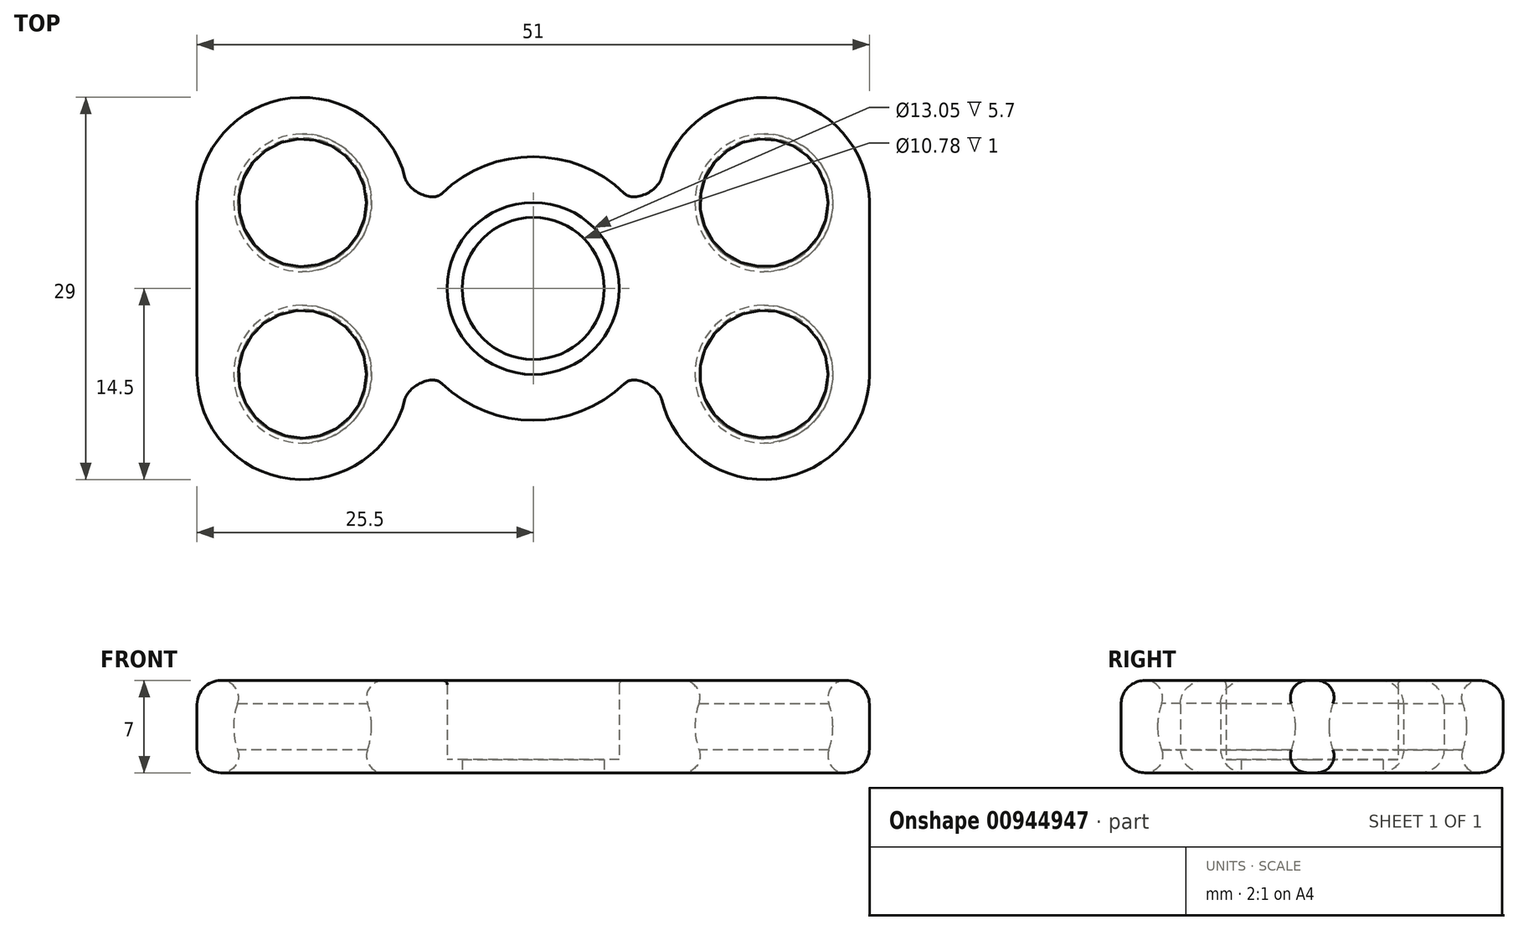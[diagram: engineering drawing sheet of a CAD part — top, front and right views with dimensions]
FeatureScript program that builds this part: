
annotation { "Feature Type Name" : "Feature", "Feature Type Description" : "" }
export const myFeature = defineFeature(function(context is Context, id is Id, definition is map)
    precondition{}
    {
        {
            var Q0;
            Q0=qCreatedBy(makeId("Top.planeOp"),FACE);
            var sketch = newSketch(context, id + "F0", { "sketchPlane" : qUnion([Q0])});
            skCircle(sketch, "E0", {"center": v(0, 0) * mm, "radius": 6.53 * mm});
            skArc(sketch, "E1", {"start": v(6.91, 7.23) * mm, "mid": v(0, 10) * mm, "end": v(-6.91, 7.23) * mm});
            skCircle(sketch, "E2", {"center": v(17.5, 6.5) * mm, "radius": 2.5 * mm});
            skCircle(sketch, "E3", {"center": v(17.5, -6.5) * mm, "radius": 2.5 * mm});
            skArc(sketch, "E4", {"start": v(9.73, -8.38) * mm, "mid": v(18.45, -14.44) * mm, "end": v(25.5, -6.5) * mm});
            skLineSegment(sketch, "E5", {"start": v(25.5, 6.5) * mm, "end": v(25.5, -6.5) * mm});
            skArc(sketch, "E6", {"start": v(7.68, 6.95) * mm, "mid": v(8.76, 7.29) * mm, "end": v(9.59, 8.07) * mm});
            skArc(sketch, "E7", {"start": v(9.59, -8.07) * mm, "mid": v(8.76, -7.29) * mm, "end": v(7.68, -6.95) * mm});
            skArc(sketch, "E8.trimOffspring", {"start": v(25.5, 6.5) * mm, "mid": v(18.45, 14.44) * mm, "end": v(9.73, 8.38) * mm});
            skLineSegment(sketch, "E9", {"start": v(0, 15.27) * mm, "end": v(0, -14.8) * mm});
            skPoint(sketch, "E10.visualSharp", {"position": v(7.18, 6.96) * mm});
            skArc(sketch, "E10.filletArc", {"start": v(6.91, 7.23) * mm, "mid": v(7.27, 7) * mm, "end": v(7.68, 6.95) * mm});
            skPoint(sketch, "E11.visualSharp", {"position": v(9.7, 8.24) * mm});
            skArc(sketch, "E11.filletArc", {"start": v(9.59, 8.07) * mm, "mid": v(9.67, 8.22) * mm, "end": v(9.73, 8.38) * mm});
            skPoint(sketch, "E12.visualSharp", {"position": v(7.18, -6.96) * mm});
            skArc(sketch, "E12.filletArc", {"start": v(7.68, -6.95) * mm, "mid": v(7.27, -7) * mm, "end": v(6.91, -7.23) * mm});
            skPoint(sketch, "E13.visualSharp", {"position": v(9.7, -8.24) * mm});
            skArc(sketch, "E13.filletArc", {"start": v(9.73, -8.38) * mm, "mid": v(9.67, -8.22) * mm, "end": v(9.59, -8.07) * mm});
            skArc(sketch, "E14.MirrorCS", {"start": v(-9.73, -8.38) * mm, "mid": v(-9.67, -8.22) * mm, "end": v(-9.59, -8.07) * mm});
            skArc(sketch, "E15.MirrorCS", {"start": v(-7.68, 6.95) * mm, "mid": v(-8.76, 7.29) * mm, "end": v(-9.59, 8.07) * mm});
            skArc(sketch, "E16.MirrorCS", {"start": v(-6.91, 7.23) * mm, "mid": v(-7.27, 7) * mm, "end": v(-7.68, 6.95) * mm});
            skArc(sketch, "E17.MirrorCS", {"start": v(-9.59, 8.07) * mm, "mid": v(-9.67, 8.22) * mm, "end": v(-9.73, 8.38) * mm});
            skArc(sketch, "E18.MirrorCS", {"start": v(-7.68, -6.95) * mm, "mid": v(-7.27, -7) * mm, "end": v(-6.91, -7.23) * mm});
            skArc(sketch, "E19.MirrorCS", {"start": v(-9.59, -8.07) * mm, "mid": v(-8.76, -7.29) * mm, "end": v(-7.68, -6.95) * mm});
            skPoint(sketch, "E20.MirrorP", {"position": v(-9.7, 8.24) * mm});
            skPoint(sketch, "E21.MirrorP", {"position": v(-7.18, -6.96) * mm});
            skCircle(sketch, "E22.MirrorC", {"center": v(-17.5, -6.5) * mm, "radius": 2.5 * mm});
            skArc(sketch, "E23.MirrorCS", {"start": v(-25.5, 6.5) * mm, "mid": v(-18.45, 14.44) * mm, "end": v(-9.73, 8.38) * mm});
            skLineSegment(sketch, "E24.MirrorCS", {"start": v(-25.5, 6.5) * mm, "end": v(-25.5, -6.5) * mm});
            skPoint(sketch, "E25.MirrorP", {"position": v(-9.7, -8.24) * mm});
            skArc(sketch, "E26.MirrorCS", {"start": v(-9.73, -8.38) * mm, "mid": v(-18.45, -14.44) * mm, "end": v(-25.5, -6.5) * mm});
            skCircle(sketch, "E27.MirrorC", {"center": v(-17.5, 6.5) * mm, "radius": 2.5 * mm});
            skPoint(sketch, "E28.MirrorP", {"position": v(-7.18, 6.96) * mm});
            skArc(sketch, "E29.trimOffspring", {"start": v(-6.91, -7.23) * mm, "mid": v(0, -10) * mm, "end": v(6.91, -7.23) * mm});
            skSolve(sketch);
        }
        {
            var Q0;
            Q0=qSketchRegion(id+"F0",true);
            extrude(context, id + "F1", {"entities" : qUnion([Q0]), "depth" : 3.5 * mm, "offsetDistance" : 25 * mm});
        }
        {
            var Q0;
            Q0=qSketchRegion(id+"F0",true);
            extrude(context, id + "F2", {"entities" : qUnion([Q0]), "operationType" : NewBodyOperationType.ADD, "oppositeDirection" : true, "depth" : 3.5 * mm, "offsetDistance" : 25 * mm});
        }
        {
            var Q0;
            Q0=qCreatedBy(makeId("Top.planeOp"),FACE);
            var sketch = newSketch(context, id + "F3", { "sketchPlane" : qUnion([Q0])});
            skArc(sketch, "E30", {"start": v(-17.5, 11.73) * mm, "mid": v(-22.73, 6.5) * mm, "end": v(-17.5, 1.27) * mm});
            skLineSegment(sketch, "E31", {"start": v(-17.5, 11.73) * mm, "end": v(-17.5, 1.27) * mm});
            skSolve(sketch);
        }
        {
            var Q0;
            Q0=qSketchRegion(id+"F3",true);
            var Q1;
            Q1=sQuery(id+"F3.wireOp",EDGE,"E31");
            revolve(context, id + "F4", {"operationType" : NewBodyOperationType.REMOVE, "surfaceOperationType" : NewSurfaceOperationType.NEW, "entities" : qUnion([Q0]), "axis" : qUnion([Q1]), "revolveType" : RevolveType.FULL, "oppositeDirection" : true});
        }
        {
            var Q0;
            Q0=qCreatedBy(makeId("Top.planeOp"),FACE);
            var sketch = newSketch(context, id + "F5", { "sketchPlane" : qUnion([Q0])});
            skArc(sketch, "E32", {"start": v(-17.5, -1.27) * mm, "mid": v(-22.73, -6.5) * mm, "end": v(-17.5, -11.73) * mm});
            skLineSegment(sketch, "E33", {"start": v(-17.5, -1.27) * mm, "end": v(-17.5, -11.73) * mm});
            skSolve(sketch);
        }
        {
            var Q0;
            Q0=makeQuery(id+"F5.imprint","IMPRINT",FACE,{"disambiguationData":[TD([[makeQuery(id+"F5.imprint","IMPRINT",EDGE,{"derivedFrom":sQuery(id+"F5.wireOp",EDGE,"E32")}),1.0]])]});
            var Q1;
            Q1=sQuery(id+"F5.wireOp",EDGE,"E33");
            revolve(context, id + "F6", {"operationType" : NewBodyOperationType.REMOVE, "surfaceOperationType" : NewSurfaceOperationType.NEW, "entities" : qUnion([Q0]), "axis" : qUnion([Q1]), "revolveType" : RevolveType.FULL, "oppositeDirection" : true});
        }
        {
            var Q0;
            Q0=qCreatedBy(makeId("Top.planeOp"),FACE);
            var sketch = newSketch(context, id + "F7", { "sketchPlane" : qUnion([Q0])});
            skArc(sketch, "E34", {"start": v(17.5, 11.73) * mm, "mid": v(12.27, 6.5) * mm, "end": v(17.5, 1.27) * mm});
            skLineSegment(sketch, "E35", {"start": v(17.5, 11.73) * mm, "end": v(17.5, 1.27) * mm});
            skSolve(sketch);
        }
        {
            var Q0;
            Q0=makeQuery(id+"F7.imprint","IMPRINT",FACE,{"disambiguationData":[TD([[makeQuery(id+"F7.imprint","IMPRINT",EDGE,{"derivedFrom":sQuery(id+"F7.wireOp",EDGE,"E34")}),1.0]])]});
            var Q1;
            Q1=sQuery(id+"F7.wireOp",EDGE,"E35");
            revolve(context, id + "F8", {"operationType" : NewBodyOperationType.REMOVE, "surfaceOperationType" : NewSurfaceOperationType.NEW, "entities" : qUnion([Q0]), "axis" : qUnion([Q1]), "revolveType" : RevolveType.FULL, "oppositeDirection" : true});
        }
        {
            var Q0;
            Q0=qCreatedBy(makeId("Top.planeOp"),FACE);
            var sketch = newSketch(context, id + "F9", { "sketchPlane" : qUnion([Q0])});
            skArc(sketch, "E36", {"start": v(17.5, -1.27) * mm, "mid": v(12.27, -6.5) * mm, "end": v(17.5, -11.73) * mm});
            skLineSegment(sketch, "E37", {"start": v(17.5, -1.27) * mm, "end": v(17.5, -11.73) * mm});
            skSolve(sketch);
        }
        {
            var Q0;
            Q0=makeQuery(id+"F9.imprint","IMPRINT",FACE,{"disambiguationData":[TD([[makeQuery(id+"F9.imprint","IMPRINT",EDGE,{"derivedFrom":sQuery(id+"F9.wireOp",EDGE,"E36")}),1.0]])]});
            var Q1;
            Q1=sQuery(id+"F9.wireOp",EDGE,"E37");
            revolve(context, id + "F10", {"operationType" : NewBodyOperationType.REMOVE, "surfaceOperationType" : NewSurfaceOperationType.NEW, "entities" : qUnion([Q0]), "axis" : qUnion([Q1]), "revolveType" : RevolveType.FULL, "oppositeDirection" : true});
        }
        {
            var Q0;
            Q0=makeQuery(id+"F2.opExtrude","CAP_EDGE",EDGE,{"disambiguationData":[OSD([sQuery(id+"F0.wireOp",EDGE,"E1")])],"isStart":false});
            var Q1;
            Q1=makeQuery(id+"F1.opExtrude","CAP_EDGE",EDGE,{"disambiguationData":[OSD([sQuery(id+"F0.wireOp",EDGE,"E1")])],"isStart":false});
            fillet(context, id + "F11", {"entities" : qUnion([Q0, Q1]), "radius" : 1.8 * mm, "tangentPropagation" : true, "allowEdgeOverflow" : false});
        }
        {
            var Q0;
            Q0=makeQuery(id+"F4.boolean.opBoolean","COPY",FACE,{"derivedFrom":makeQuery(id+"F4.opRevolve","SWEPT_FACE",FACE,{"disambiguationData":[OSD([sQuery(id+"F3.wireOp",EDGE,"E30")])]})});
            var Q1;
            Q1=makeQuery(id+"F6.boolean.opBoolean","COPY",FACE,{"derivedFrom":makeQuery(id+"F6.opRevolve","SWEPT_FACE",FACE,{"disambiguationData":[OSD([sQuery(id+"F5.wireOp",EDGE,"E32")])]})});
            var Q2;
            Q2=makeQuery(id+"F8.boolean.opBoolean","COPY",FACE,{"derivedFrom":makeQuery(id+"F8.opRevolve","SWEPT_FACE",FACE,{"disambiguationData":[OSD([sQuery(id+"F7.wireOp",EDGE,"E34")])]})});
            var Q3;
            Q3=makeQuery(id+"F10.boolean.opBoolean","COPY",FACE,{"derivedFrom":makeQuery(id+"F10.opRevolve","SWEPT_FACE",FACE,{"disambiguationData":[OSD([sQuery(id+"F9.wireOp",EDGE,"E36")])]})});
            fillet(context, id + "F12", {"entities" : qUnion([Q0, Q1, Q2, Q3]), "radius" : 1.3 * mm, "tangentPropagation" : true, "allowEdgeOverflow" : false});
        }
        {
            var Q0;
            Q0=makeQuery(id+"F1.opExtrude","CAP_EDGE",EDGE,{"disambiguationData":[OSD([sQuery(id+"F0.wireOp",EDGE,"E0")])],"isStart":false});
            fillet(context, id + "F13", {"entities" : qUnion([Q0]), "radius" : .3 * mm, "tangentPropagation" : true, "allowEdgeOverflow" : false});
        }
        {
            var Q0;
            Q0=makeQuery(id+"F2.opExtrude","CAP_FACE",FACE,{"disambiguationData":[OSD([sQuery(id+"F0.wireOp",EDGE,"E0"),sQuery(id+"F0.wireOp",EDGE,"E1"),sQuery(id+"F0.wireOp",EDGE,"E2"),sQuery(id+"F0.wireOp",EDGE,"E3"),sQuery(id+"F0.wireOp",EDGE,"E4"),sQuery(id+"F0.wireOp",EDGE,"E5"),sQuery(id+"F0.wireOp",EDGE,"E6"),sQuery(id+"F0.wireOp",EDGE,"E7"),sQuery(id+"F0.wireOp",EDGE,"E8.trimOffspring"),sQuery(id+"F0.wireOp",EDGE,"E10.filletArc"),sQuery(id+"F0.wireOp",EDGE,"E11.filletArc"),sQuery(id+"F0.wireOp",EDGE,"E12.filletArc"),sQuery(id+"F0.wireOp",EDGE,"E13.filletArc"),sQuery(id+"F0.wireOp",EDGE,"E14.MirrorCS"),sQuery(id+"F0.wireOp",EDGE,"E15.MirrorCS"),sQuery(id+"F0.wireOp",EDGE,"E16.MirrorCS"),sQuery(id+"F0.wireOp",EDGE,"E17.MirrorCS"),sQuery(id+"F0.wireOp",EDGE,"E18.MirrorCS"),sQuery(id+"F0.wireOp",EDGE,"E19.MirrorCS"),sQuery(id+"F0.wireOp",EDGE,"E22.MirrorC"),sQuery(id+"F0.wireOp",EDGE,"E23.MirrorCS"),sQuery(id+"F0.wireOp",EDGE,"E24.MirrorCS"),sQuery(id+"F0.wireOp",EDGE,"E26.MirrorCS"),sQuery(id+"F0.wireOp",EDGE,"E27.MirrorC"),sQuery(id+"F0.wireOp",EDGE,"E29.trimOffspring")])],"isStart":false});
            var sketch = newSketch(context, id + "F14", { "sketchPlane" : qUnion([Q0])});
            skCircle(sketch, "E38", {"center": v(0, 0) * mm, "radius": 5.39 * mm});
            skSolve(sketch);
        }
        {
            var Q0;
            Q0=makeQuery(id+"F14.imprint","IMPRINT",FACE,{"disambiguationData":[TD([[makeQuery(id+"F14.imprint","IMPRINT",EDGE,{"derivedFrom":sQuery(id+"F14.wireOp",EDGE,"E38")}),-1.0]])]});
            extrude(context, id + "F15", {"entities" : qUnion([Q0]), "operationType" : NewBodyOperationType.ADD, "oppositeDirection" : true, "depth" : 1 * mm, "offsetDistance" : 25 * mm});
        }
    });
